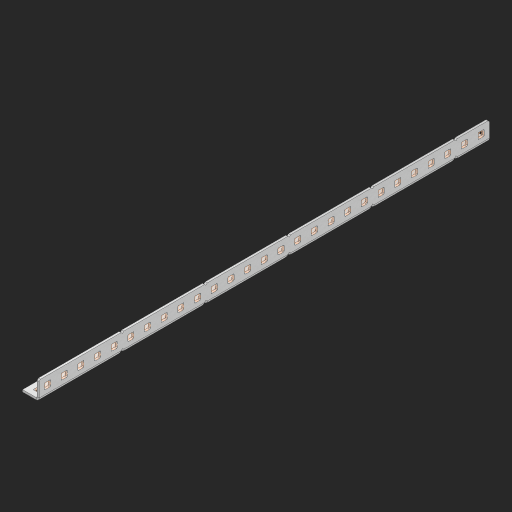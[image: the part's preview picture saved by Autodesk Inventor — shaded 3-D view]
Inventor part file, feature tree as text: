
AUTODESK INVENTOR PART (.ipt)
format: ipt  version: 2023 (Build 270158000, 158)  size: 900,096 bytes
history: native  units: in
note: dims shown in document units (in); Inventor stores cm internally (conversion verified against a paired STEP export)
features: other x59, extrude x53, sheet_metal_op x10, sketch x8, mirror x1, pattern_linear x1, chamfer x1
ambient origin geometry x8: Origin, YZ Plane, XZ Plane, XY Plane, X Axis, Y Axis, Z Axis, Center Point
bodies: Solid1 (feature_tree), Body (feature_tree)
feature tree (133):
  other  "Flange Pattern Plane"
  sheet_metal_op  "Flange Pattern"
  sheet_metal_op  "Body Pattern"
  other  "Arc Length"
  mirror  "Notch Mirror"
  pattern_linear  "Notch Pattern"  Spacing1=0.25in  [1 undecoded]
  chamfer  "End Chamfer"
  extrude  "Half Cut"  Depth=0.0625in
  sketch  "Sketch1"  dims[d0=1.5in]
  other  "Plate1"
  sketch  "Sketch2"  dims[d1=13.5in]
  other  "Plate2"
  sheet_metal_op  "Bend1"
  sheet_metal_op  "Corner1"
  sketch  "Sketch3"  dims[d2=0.0625in]
  other  "Flange Pattern Sketch"
  sketch  "Sketch7"  dims[d3=0.0625in]
  other  "Srf1"
  other  "Srf2"
  sketch  "Sketch8"  dims[d4=0.0312in]
  sketch  "Sketch9"  dims[d5=0.125in]
  other  "Srf91"
  sheet_metal_op  "Body Pattern Sketch"
  other  "Srf92"
  sketch  "Sketch13"  dims[d6=0.0625in]
  sketch  "Sketch14"  dims[d7=0.5in d8=90.0deg d9=0.0312in d10=0.25in d11=0.0625in d12=0.0625in d16=0.182in d17=0.02in d18=0.0625in d19=0.0in d20=0.25in d21=0.25in d46=0.172in d47=1.0in d48=0.0in d49=0.182in d50=0.02in d51=0.25in d52=0.25in d53=0.0625in d54=0.0in d55=0.172in d56=1.0in d57=0.0in d60=10.6299in d62=0.5in d63=0.3937in d65=0.5in d85=0.1473in d86=0.1782in d88=0.04in d89=0.0625in d90=0.0in d91=0.04in d92=0.0491in d95=2.5in d96=0.04in d97=0.25in d98=45.0deg d101=0.0in d102=2.497in d131=0.5in d132=10.6299in d134=0.5in d139=0.5in]
  other  "Srf856"
  other  "Srf1310"
  other  "Srf1311"
  other  "Srf1312"
  other  "Srf1376"
  other  "Srf1377"
  other  "Srf1728"
  other  "Srf1755"
  other  "Srf1878"
  other  "Srf1879"
  other  "Srf1880"
  other  "Srf1881"
  other  "Srf1882"
  other  "Srf1883"
  other  "Srf1884"
  other  "Srf1885"
  other  "Srf1886"
  other  "Srf1887"
  other  "Srf1888"
  other  "Srf1889"
  other  "Srf1890"
  other  "Srf1891"
  other  "Srf1892"
  other  "Srf1893"
  other  "Srf1894"
  other  "Srf1895"
  other  "Srf1896"
  other  "Srf1897"
  other  "Srf1898"
  other  "Srf1942"
  other  "Srf1943"
  other  "Srf1944"
  other  "Srf1945"
  other  "Srf1946"
  other  "Srf1947"
  other  "Srf1948"
  other  "Srf1949"
  other  "Srf1950"
  other  "Srf1951"
  other  "Srf1952"
  other  "Srf1953"
  other  "Srf1954"
  other  "Srf1955"
  other  "Srf1956"
  other  "Srf1957"
  other  "Srf1958"
  other  "Srf1959"
  other  "Srf1960"
  other  "Srf1961"
  other  "Srf1962"
  sheet_metal_op  "Flange Stamp"
  sheet_metal_op  "Flange Circle"
  sheet_metal_op  "Body Stamp"
  sheet_metal_op  "Body Circle"
  sheet_metal_op  "Notch"
  extrude  "ExtrusionSrf2"  Depth=0.0625in
  extrude  "ExtrusionSrf92"  Depth=0.5in
  extrude  "ExtrusionSrf856"  Depth=0.02in
  extrude  "ExtrusionSrf1310"  Depth=0.0625in
  extrude  "ExtrusionSrf1311"  TaperAngle=0.0deg  [1 undecoded]
  extrude  "ExtrusionSrf1312"  Depth=0.5in
  extrude  "ExtrusionSrf1376"  Depth=0.5in
  extrude  "ExtrusionSrf1377"  Depth=0.5in
  extrude  "ExtrusionSrf1728"  Depth=0.5in TaperAngle=0.0deg
  extrude  "ExtrusionSrf1755"  Depth=0.5in
  extrude  "ExtrusionSrf1878"  Depth=0.02in
  extrude  "ExtrusionSrf1879"  Depth=0.5in
  extrude  "ExtrusionSrf1880"  Depth=0.5in
  extrude  "ExtrusionSrf1881"  Depth=0.0625in
  extrude  "ExtrusionSrf1882"  TaperAngle=0.0deg  [1 undecoded]
  extrude  "ExtrusionSrf1883"  Depth=0.5in
  extrude  "ExtrusionSrf1884"  Depth=0.5in TaperAngle=0.0deg
  extrude  "ExtrusionSrf1885"  Depth=0.5in
  extrude  "ExtrusionSrf1886"  Depth=0.5in
  extrude  "ExtrusionSrf1887"  Depth=0.5in
  extrude  "ExtrusionSrf1888"  Depth=0.5in
  extrude  "ExtrusionSrf1889"  Depth=0.5in
  extrude  "ExtrusionSrf1890"  Depth=0.0625in
  extrude  "ExtrusionSrf1891"  TaperAngle=0.0deg  [1 undecoded]
  extrude  "ExtrusionSrf1892"  Depth=0.5in
  extrude  "ExtrusionSrf1893"  Depth=0.5in
  extrude  "ExtrusionSrf1894"  Depth=0.5in
  extrude  "ExtrusionSrf1895"  Depth=0.5in TaperAngle=45.0deg
  extrude  "ExtrusionSrf1896"  TaperAngle=0.0deg  [1 undecoded]
  extrude  "ExtrusionSrf1897"  Depth=0.5in
  extrude  "ExtrusionSrf1898"  Depth=0.5in
  extrude  "ExtrusionSrf1942"  Depth=0.5in
  extrude  "ExtrusionSrf1943"  Depth=0.5in
  extrude  "ExtrusionSrf1944"  Depth=0.5in
  extrude  "ExtrusionSrf1945"  [1 undecoded]
  extrude  "ExtrusionSrf1946"  [1 undecoded]
  extrude  "ExtrusionSrf1947"  [1 undecoded]
  extrude  "ExtrusionSrf1948"  [1 undecoded]
  extrude  "ExtrusionSrf1949"  [1 undecoded]
  extrude  "ExtrusionSrf1950"  [1 undecoded]
  extrude  "ExtrusionSrf1951"  [1 undecoded]
  extrude  "ExtrusionSrf1952"  [1 undecoded]
  extrude  "ExtrusionSrf1953"  [1 undecoded]
  extrude  "ExtrusionSrf1954"  [1 undecoded]
  extrude  "ExtrusionSrf1955"  [1 undecoded]
  extrude  "ExtrusionSrf1956"  [1 undecoded]
  extrude  "ExtrusionSrf1957"  [1 undecoded]
  extrude  "ExtrusionSrf1958"  [1 undecoded]
  extrude  "ExtrusionSrf1959"  [1 undecoded]
  extrude  "ExtrusionSrf1960"  [1 undecoded]
  extrude  "ExtrusionSrf1961"  [1 undecoded]
  extrude  "ExtrusionSrf1962"  [1 undecoded]
note: 23 required parameter values undecoded (feature->parameter linkage not recoverable at this tier; creation-order binding heuristic only, values carry confidence <= 0.55)
